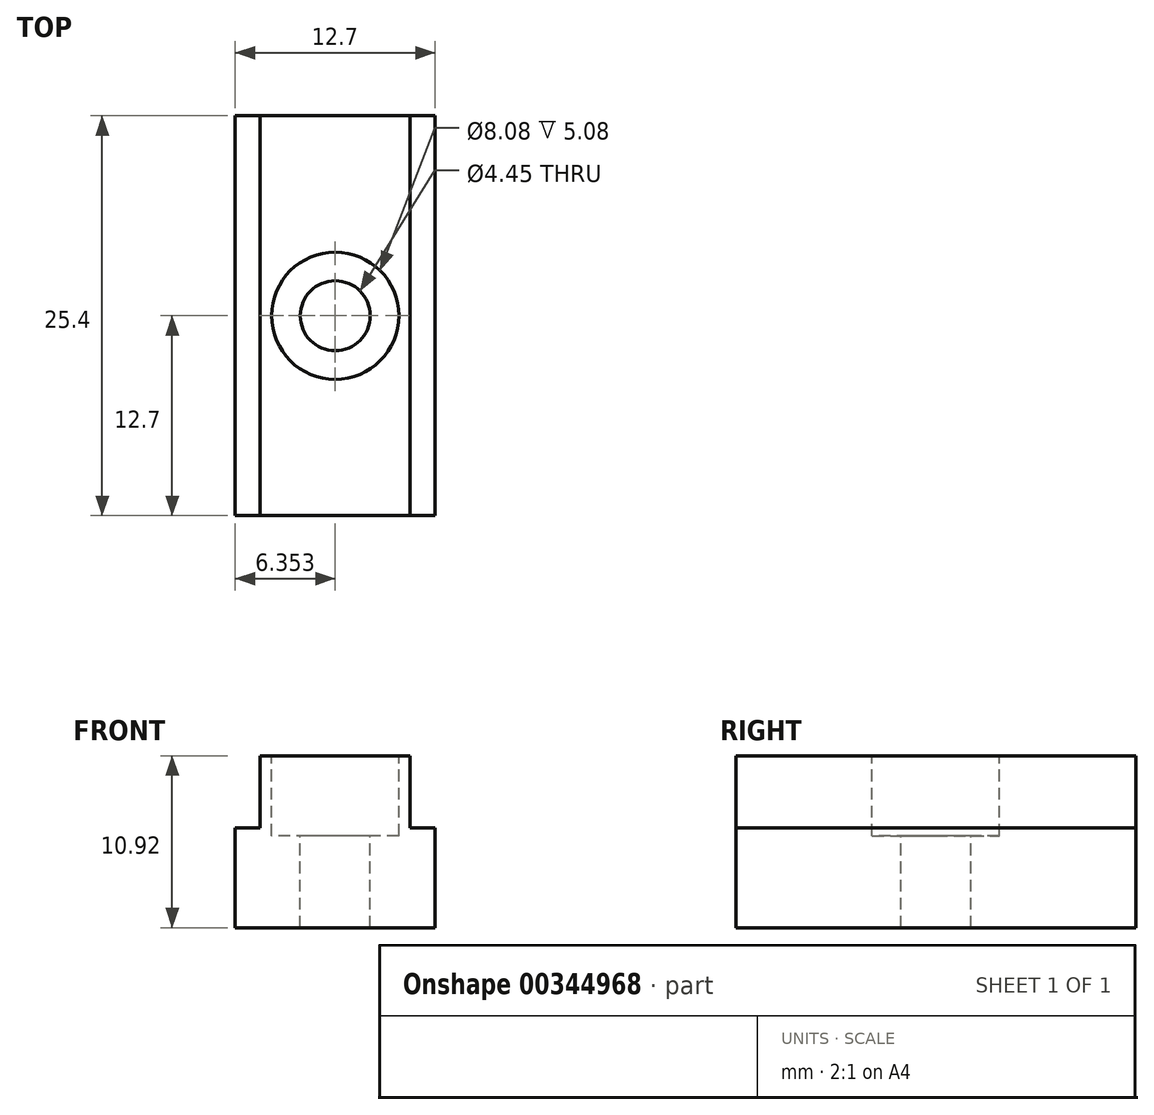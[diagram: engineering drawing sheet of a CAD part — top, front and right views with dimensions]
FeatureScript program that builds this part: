
annotation { "Feature Type Name" : "Feature", "Feature Type Description" : "" }
export const myFeature = defineFeature(function(context is Context, id is Id, definition is map)
    precondition{}
    {
        {
            var Q0;
            Q0=qCreatedBy(makeId("Front.planeOp"),FACE);
            var sketch = newSketch(context, id + "F0", { "sketchPlane" : qUnion([Q0])});
            skLineSegment(sketch, "E0.bottom", {"start": v(0, 4.57) * mm, "end": v(9.52, 4.57) * mm});
            skLineSegment(sketch, "E0.top", {"start": v(0, 0) * mm, "end": v(9.52, 0) * mm});
            skLineSegment(sketch, "E0.left", {"start": v(0, 4.57) * mm, "end": v(0, 0) * mm});
            skLineSegment(sketch, "E0.right", {"start": v(9.52, 4.57) * mm, "end": v(9.52, 0) * mm});
            skLineSegment(sketch, "E1.bottom", {"start": v(-1.59, -6.35) * mm, "end": v(11.11, -6.35) * mm});
            skLineSegment(sketch, "E1.top", {"start": v(-1.59, 0) * mm, "end": v(11.11, 0) * mm});
            skLineSegment(sketch, "E1.left", {"start": v(-1.59, -6.35) * mm, "end": v(-1.59, 0) * mm});
            skLineSegment(sketch, "E1.right", {"start": v(11.11, -6.35) * mm, "end": v(11.11, 0) * mm});
            skLineSegment(sketch, "E2", {"start": v(11.11, -3.18) * mm, "end": v(-1.59, -3.18) * mm, "construction": true});
            skLineSegment(sketch, "E3", {"start": v(4.76, 0) * mm, "end": v(4.76, -6.35) * mm, "construction": true});
            skLineSegment(sketch, "E4", {"start": v(4.76, 0) * mm, "end": v(4.76, 4.57) * mm, "construction": true});
            skSolve(sketch);
        }
        {
            var Q0;
            Q0=makeQuery(id+"F0.imprint","IMPRINT",FACE,{"disambiguationData":[TD([[makeQuery(id+"F0.imprint","IMPRINT",EDGE,{"derivedFrom":sQuery(id+"F0.wireOp",EDGE,"E0.bottom")}),-1.0]])]});
            var Q1;
            Q1=makeQuery(id+"F0.imprint","IMPRINT",FACE,{"disambiguationData":[TD([[makeQuery(id+"F0.imprint","IMPRINT",EDGE,{"derivedFrom":sQuery(id+"F0.wireOp",EDGE,"E1.bottom")}),1.0]])]});
            extrude(context, id + "F1", {"entities" : qUnion([Q0, Q1]), "depth" : 25.4 * mm});
        }
        {
            var Q0;
            Q0=makeQuery(id+"F1.opExtrude","SWEPT_FACE",FACE,{"disambiguationData":[OSD([sQuery(id+"F0.wireOp",EDGE,"E0.bottom")])]});
            var sketch = newSketch(context, id + "F2", { "sketchPlane" : qUnion([Q0])});
            skCircle(sketch, "E5", {"center": v(4.76, -12.7) * mm, "radius": 4.04 * mm});
            skSolve(sketch);
        }
        {
            var Q0;
            Q0=makeQuery(id+"F2.imprint","IMPRINT",FACE,{"disambiguationData":[TD([[makeQuery(id+"F2.imprint","IMPRINT",EDGE,{"derivedFrom":sQuery(id+"F2.wireOp",EDGE,"E5")}),1.0]])]});
            extrude(context, id + "F3", {"entities" : qUnion([Q0]), "operationType" : NewBodyOperationType.REMOVE, "oppositeDirection" : true, "depth" : 5.08 * mm});
        }
        {
            var Q0;
            Q0=makeQuery(id+"F3.boolean.opBoolean","COPY",FACE,{"derivedFrom":makeQuery(id+"F3.opExtrude","CAP_FACE",FACE,{"disambiguationData":[OSD([sQuery(id+"F2.wireOp",EDGE,"E5")])],"isStart":false})});
            var sketch = newSketch(context, id + "F4", { "sketchPlane" : qUnion([Q0])});
            skCircle(sketch, "E6", {"center": v(4.76, -12.7) * mm, "radius": 2.22 * mm});
            skSolve(sketch);
        }
        {
            var Q0;
            Q0=makeQuery(id+"F4.imprint","IMPRINT",FACE,{"disambiguationData":[TD([[makeQuery(id+"F4.imprint","IMPRINT",EDGE,{"derivedFrom":sQuery(id+"F4.wireOp",EDGE,"E6")}),1.0]])]});
            extrude(context, id + "F5", {"entities" : qUnion([Q0]), "operationType" : NewBodyOperationType.REMOVE, "endBound" : BoundingType.THROUGH_ALL, "oppositeDirection" : true, "depth" : 25.4 * mm});
        }
    });
